# Revit family: Chatham Cove 3 Sided
name_source: partatom
category: Furniture
units: mm (PartAtom-declared; Revit-internal decimal feet)

## family parameters
Always vertical = Yes
Cut with Voids When Loaded = No
OmniClass Number = 23.40.20.00
OmniClass Title = General Furniture and Specialties
Room Calculation Point = No
Shared = No
Work Plane-Based = No

## types (12) — shared parameters
Default Elevation = 0' - 0"
Manufacturer = AIS Inc
Product = CHATHAM 3-SIDED COVES
URL = https://www.ais-inc.com

## per-type parameters (varying)
| type | Description |
| F-CC3NL344230 | 42Wx30Dx34H Configurable Chatham Cove 3-Sided Left Non-Powered Options |
| F-CC3NL504230 | 42Wx30Dx50H Configurable Chatham Cove 3-Sided Left Non-Powered Options |
| F-CC3NL584230 | 42Wx30Dx58H Configurable Chatham Cove 3-Sided Left Non-Powered Options |
| F-CC3NR344230 | 42Wx30Dx34H Configurable  Chatham Cove 3-Sided Right Non-Powered Options |
| F-CC3NR504230 | 42Wx30Dx50H Configurable  Chatham Cove 3-Sided Right Non-Powered Options |
| F-CC3NR584230 | 42Wx30Dx58H Configurable  Chatham Cove 3-Sided Right Non-Powered Options |
| F-CC3PL344230 | 42Wx30Dx34H Configurable Chatham Cove 3-Sided Left Powered Options |
| F-CC3PL504230 | 42Wx30Dx50H Configurable Chatham Cove 3-Sided Left Powered Options |
| F-CC3PL584230 | 42Wx30Dx58H Configurable Chatham Cove 3-Sided Left Powered Options |
| F-CC3PR344230 | 42Wx30Dx34H Configurable Chatham Cove 3-Sided Right Powered Options |
| F-CC3PR504230 | 42Wx30Dx50H Configurable Chatham Cove 3-Sided Right Powered Options |
| F-CC3PR584230 | 42Wx30Dx58H Configurable Chatham Cove 3-Sided Right Powered Options |

note: column(s) folded — value = type name in every type: Model

type visibility flags: 12 boolean params named "<type name>" — each type sets only its own to Yes (folded from table)

## geometry (parser evidence)
native form markers: Sweep x3
no freeform markers — native parametric forms only
